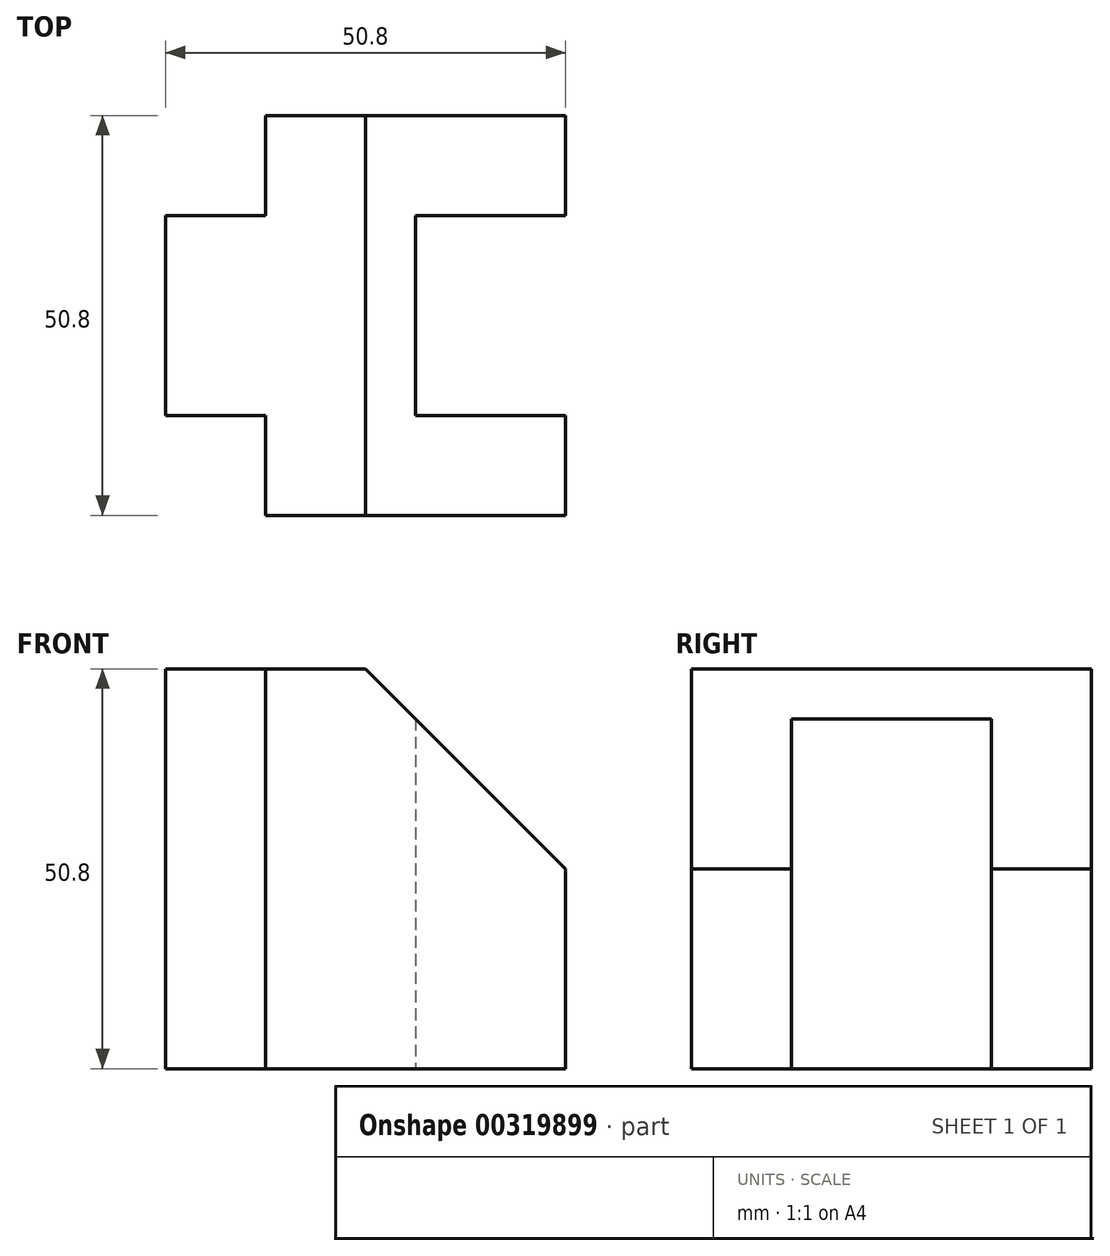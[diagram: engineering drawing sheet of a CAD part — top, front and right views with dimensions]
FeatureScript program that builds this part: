
annotation { "Feature Type Name" : "Feature", "Feature Type Description" : "" }
export const myFeature = defineFeature(function(context is Context, id is Id, definition is map)
    precondition{}
    {
        {
            var Q0;
            Q0=qCreatedBy(makeId("Front.planeOp"),FACE);
            var sketch = newSketch(context, id + "F0", { "sketchPlane" : qUnion([Q0])});
            skLineSegment(sketch, "E0", {"start": v(0, 0) * mm, "end": v(50.8, 0) * mm});
            skLineSegment(sketch, "E1", {"start": v(50.8, 0) * mm, "end": v(50.8, 25.4) * mm});
            skLineSegment(sketch, "E2", {"start": v(0, 0) * mm, "end": v(0, 50.8) * mm});
            skLineSegment(sketch, "E3", {"start": v(0, 50.8) * mm, "end": v(25.4, 50.8) * mm});
            skLineSegment(sketch, "E4", {"start": v(25.4, 50.8) * mm, "end": v(50.8, 25.4) * mm});
            skSolve(sketch);
        }
        {
            var Q0;
            Q0=makeQuery(id+"F0.imprint","IMPRINT",FACE,{"disambiguationData":[TD([[makeQuery(id+"F0.imprint","IMPRINT",EDGE,{"derivedFrom":sQuery(id+"F0.wireOp",EDGE,"E0")}),1.0]])]});
            extrude(context, id + "F1", {"entities" : qUnion([Q0]), "oppositeDirection" : true, "depth" : 50.8 * mm});
        }
        {
            var Q0;
            Q0=makeQuery(id+"F1.opExtrude","SWEPT_FACE",FACE,{"disambiguationData":[OSD([sQuery(id+"F0.wireOp",EDGE,"E0")])]});
            var sketch = newSketch(context, id + "F2", { "sketchPlane" : qUnion([Q0])});
            skLineSegment(sketch, "E5", {"start": v(50.8, -38.1) * mm, "end": v(31.75, -38.1) * mm});
            skLineSegment(sketch, "E6", {"start": v(31.75, -38.1) * mm, "end": v(31.75, -12.7) * mm});
            skLineSegment(sketch, "E7", {"start": v(31.75, -12.7) * mm, "end": v(50.8, -12.7) * mm});
            skLineSegment(sketch, "E8", {"start": v(50.8, -12.7) * mm, "end": v(50.8, -38.1) * mm});
            skSolve(sketch);
        }
        {
            var Q0;
            Q0=makeQuery(id+"F2.imprint","IMPRINT",FACE,{"disambiguationData":[TD([[makeQuery(id+"F2.imprint","IMPRINT",EDGE,{"derivedFrom":sQuery(id+"F2.wireOp",EDGE,"E5")}),-1.0]])]});
            extrude(context, id + "F3", {"entities" : qUnion([Q0]), "operationType" : NewBodyOperationType.REMOVE, "oppositeDirection" : true, "depth" : 50.8 * mm});
        }
        {
            var Q0;
            Q0=makeQuery(id+"F1.opExtrude","SWEPT_FACE",FACE,{"disambiguationData":[OSD([sQuery(id+"F0.wireOp",EDGE,"E3")])]});
            var sketch = newSketch(context, id + "F4", { "sketchPlane" : qUnion([Q0])});
            skLineSegment(sketch, "E9", {"start": v(0, 50.8) * mm, "end": v(12.7, 50.8) * mm});
            skLineSegment(sketch, "E10", {"start": v(12.7, 50.8) * mm, "end": v(12.7, 38.1) * mm});
            skLineSegment(sketch, "E11", {"start": v(12.7, 38.1) * mm, "end": v(0, 38.1) * mm});
            skLineSegment(sketch, "E12", {"start": v(0, 38.1) * mm, "end": v(0, 50.8) * mm});
            skLineSegment(sketch, "E13", {"start": v(0, 0) * mm, "end": v(12.7, 0) * mm});
            skLineSegment(sketch, "E14", {"start": v(12.7, 0) * mm, "end": v(12.7, 12.7) * mm});
            skLineSegment(sketch, "E15", {"start": v(12.7, 12.7) * mm, "end": v(0, 12.7) * mm});
            skLineSegment(sketch, "E16", {"start": v(0, 12.7) * mm, "end": v(0, 0) * mm});
            skSolve(sketch);
        }
        {
            var Q0;
            Q0=makeQuery(id+"F4.imprint","IMPRINT",FACE,{"disambiguationData":[TD([[makeQuery(id+"F4.imprint","IMPRINT",EDGE,{"derivedFrom":sQuery(id+"F4.wireOp",EDGE,"E13")}),1.0]])]});
            var Q1;
            Q1=makeQuery(id+"F4.imprint","IMPRINT",FACE,{"disambiguationData":[TD([[makeQuery(id+"F4.imprint","IMPRINT",EDGE,{"derivedFrom":sQuery(id+"F4.wireOp",EDGE,"E9")}),-1.0]])]});
            extrude(context, id + "F5", {"entities" : qUnion([Q0, Q1]), "operationType" : NewBodyOperationType.REMOVE, "oppositeDirection" : true, "depth" : 50.8 * mm});
        }
    });
